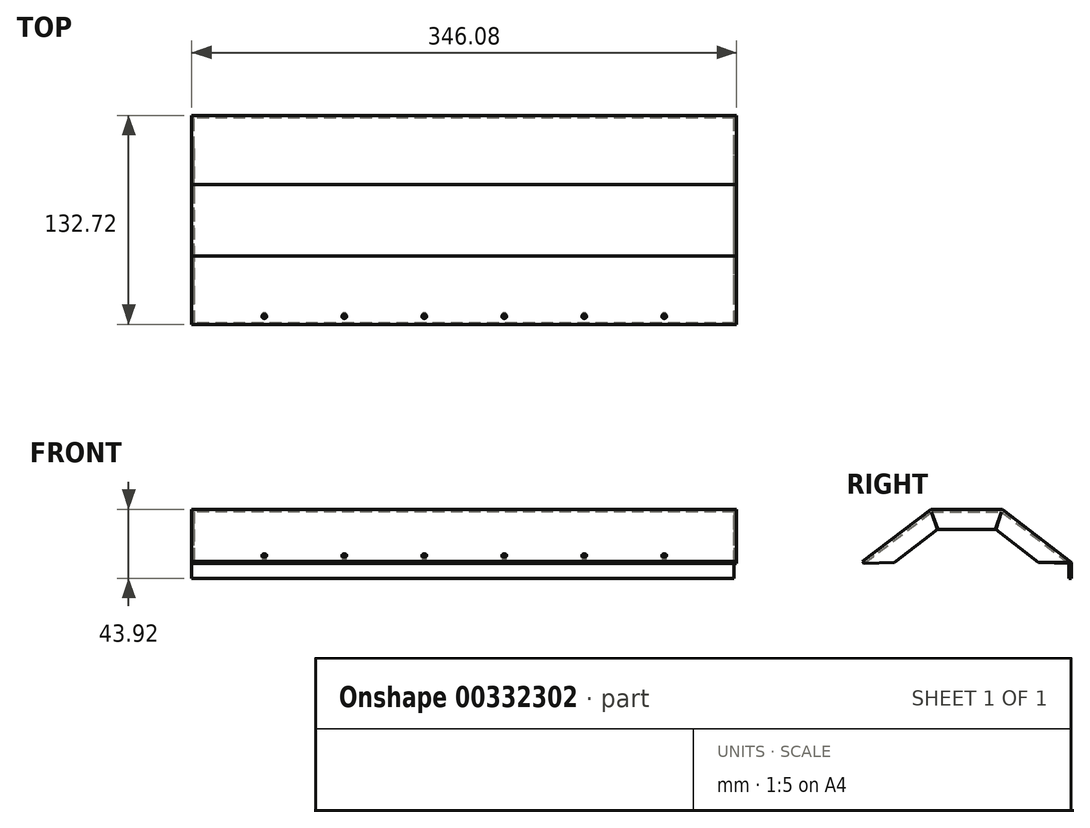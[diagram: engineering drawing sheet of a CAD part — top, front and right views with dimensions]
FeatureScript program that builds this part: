
annotation { "Feature Type Name" : "Feature", "Feature Type Description" : "" }
export const myFeature = defineFeature(function(context is Context, id is Id, definition is map)
    precondition{}
    {
        {
            var Q0;
            Q0=qCreatedBy(makeId("Right.planeOp"),FACE);
            var sketch = newSketch(context, id + "F0", { "sketchPlane" : qUnion([Q0])});
            skLineSegment(sketch, "E0", {"start": v(0, 0) * mm, "end": v(130.18, 0) * mm, "construction": true});
            skLineSegment(sketch, "E1", {"start": v(0, 0) * mm, "end": v(42.86, 32.8) * mm});
            skLineSegment(sketch, "E2", {"start": v(42.86, 32.8) * mm, "end": v(87.31, 32.8) * mm});
            skLineSegment(sketch, "E3", {"start": v(87.31, 32.8) * mm, "end": v(130.18, 0) * mm});
            skLineSegment(sketch, "E4", {"start": v(130.18, 0) * mm, "end": v(130.18, -9.53) * mm});
            skLineSegment(sketch, "E5", {"start": v(130.18, -9.53) * mm, "end": v(131.76, -9.53) * mm});
            skLineSegment(sketch, "E6.0", {"start": v(0, 1.59) * mm, "end": v(130.18, 1.59) * mm, "construction": true});
            skLineSegment(sketch, "E7", {"start": v(131.76, -9.53) * mm, "end": v(131.76, 0.78) * mm});
            skLineSegment(sketch, "E8.0", {"start": v(42.32, 34.4) * mm, "end": v(87.85, 34.4) * mm});
            skLineSegment(sketch, "E9.0", {"start": v(-0.96, 1.26) * mm, "end": v(42.32, 34.4) * mm});
            skLineSegment(sketch, "E10.0", {"start": v(87.85, 34.4) * mm, "end": v(131.76, 0.78) * mm});
            skLineSegment(sketch, "E11", {"start": v(-0.96, 1.26) * mm, "end": v(0, 0) * mm});
            skSolve(sketch);
        }
        {
            var Q0;
            Q0=makeQuery(id+"F0.imprint","IMPRINT",FACE,{"disambiguationData":[TD([[makeQuery(id+"F0.imprint","IMPRINT",EDGE,{"derivedFrom":sQuery(id+"F0.wireOp",EDGE,"E1")}),1.0]])]});
            extrude(context, id + "F1", {"entities" : qUnion([Q0]), "depth" : 342.9 * mm});
        }
        {
            var Q0;
            Q0=makeQuery(id+"F1.opExtrude","CAP_FACE",FACE,{"disambiguationData":[OSD([sQuery(id+"F0.wireOp",EDGE,"E1"),sQuery(id+"F0.wireOp",EDGE,"E2"),sQuery(id+"F0.wireOp",EDGE,"E3"),sQuery(id+"F0.wireOp",EDGE,"E4"),sQuery(id+"F0.wireOp",EDGE,"E5"),sQuery(id+"F0.wireOp",EDGE,"E7"),sQuery(id+"F0.wireOp",EDGE,"E8.0"),sQuery(id+"F0.wireOp",EDGE,"E9.0"),sQuery(id+"F0.wireOp",EDGE,"E10.0"),sQuery(id+"F0.wireOp",EDGE,"E11")])],"isStart":false});
            var sketch = newSketch(context, id + "F2", { "sketchPlane" : qUnion([Q0])});
            skLineSegment(sketch, "E12.0", {"start": v(19.36, 0.82) * mm, "end": v(46.42, 21.54) * mm});
            skLineSegment(sketch, "E13.0", {"start": v(46.88, 21.7) * mm, "end": v(83.3, 21.7) * mm});
            skLineSegment(sketch, "E14.0", {"start": v(83.75, 21.54) * mm, "end": v(110.81, 0.82) * mm});
            skLineSegment(sketch, "E15", {"start": v(19.36, 0.82) * mm, "end": v(0, 0) * mm});
            skLineSegment(sketch, "E16", {"start": v(46.88, 21.7) * mm, "end": v(42.86, 32.8) * mm});
            skLineSegment(sketch, "E17", {"start": v(42.86, 32.8) * mm, "end": v(46.42, 21.54) * mm});
            skLineSegment(sketch, "E18", {"start": v(83.3, 21.7) * mm, "end": v(87.31, 32.8) * mm});
            skLineSegment(sketch, "E19", {"start": v(87.31, 32.8) * mm, "end": v(83.75, 21.54) * mm});
            skLineSegment(sketch, "E20", {"start": v(130.18, 0) * mm, "end": v(123.42, -8.82) * mm, "construction": true});
            skLineSegment(sketch, "E21", {"start": v(110.81, 0.82) * mm, "end": v(130.18, 0) * mm});
            skSolve(sketch);
        }
        {
            var Q0;
            Q0=makeQuery(id+"F2.imprint","IMPRINT",FACE,{"disambiguationData":[TD([[makeQuery(id+"F2.imprint","IMPRINT",EDGE,{"derivedFrom":sQuery(id+"F2.wireOp",EDGE,"E12.0")}),1.0]])]});
            var Q1;
            Q1=makeQuery(id+"F2.imprint","IMPRINT",FACE,{"disambiguationData":[TD([[makeQuery(id+"F2.imprint","IMPRINT",EDGE,{"derivedFrom":sQuery(id+"F2.wireOp",EDGE,"E13.0")}),1.0]])]});
            var Q2;
            Q2=makeQuery(id+"F2.imprint","IMPRINT",FACE,{"disambiguationData":[TD([[makeQuery(id+"F2.imprint","IMPRINT",EDGE,{"derivedFrom":sQuery(id+"F2.wireOp",EDGE,"E14.0")}),1.0]])]});
            var Q3;
            Q3=makeQuery(id+"F2.imprint","IMPRINT",FACE,{"disambiguationData":[TD([[makeQuery(id+"F2.imprint","IMPRINT",EDGE,{"derivedFrom":makeQuery(id+"F1.opExtrude","CAP_EDGE",EDGE,{"disambiguationData":[OSD([sQuery(id+"F0.wireOp",EDGE,"E1")])],"isStart":false})}),1.0]])]});
            extrude(context, id + "F3", {"entities" : qUnion([Q0, Q1, Q2, Q3]), "depth" : 1.59 * mm});
        }
        {
            var Q0;
            Q0=makeQuery(id+"F3.opExtrude","SWEPT_FACE",FACE,{"disambiguationData":[OSD([sQuery(id+"F0.wireOp",EDGE,"E7")])]});
            var sketch = newSketch(context, id + "F4", { "sketchPlane" : qUnion([Q0])});
            skLineSegment(sketch, "E22.bottom", {"start": v(-344.49, 0.78) * mm, "end": v(-342.9, 0.78) * mm});
            skLineSegment(sketch, "E22.top", {"start": v(-344.49, -9.53) * mm, "end": v(-342.9, -9.53) * mm});
            skLineSegment(sketch, "E22.left", {"start": v(-344.49, 0.78) * mm, "end": v(-344.49, -9.53) * mm});
            skLineSegment(sketch, "E22.right", {"start": v(-342.9, 0.78) * mm, "end": v(-342.9, -9.53) * mm});
            skSolve(sketch);
        }
        {
            var Q0;
            Q0=makeQuery(id+"F4.imprint","IMPRINT",FACE,{"disambiguationData":[TD([[makeQuery(id+"F4.imprint","IMPRINT",EDGE,{"derivedFrom":sQuery(id+"F4.wireOp",EDGE,"E22.bottom")}),-1.0]])]});
            extrude(context, id + "F5", {"entities" : qUnion([Q0]), "operationType" : NewBodyOperationType.REMOVE, "oppositeDirection" : true, "depth" : 25.4 * mm});
        }
        {
            var Q0;
            Q0=makeQuery(id+"F1.opExtrude","CAP_FACE",FACE,{"disambiguationData":[OSD([sQuery(id+"F0.wireOp",EDGE,"E1"),sQuery(id+"F0.wireOp",EDGE,"E2"),sQuery(id+"F0.wireOp",EDGE,"E3"),sQuery(id+"F0.wireOp",EDGE,"E4"),sQuery(id+"F0.wireOp",EDGE,"E5"),sQuery(id+"F0.wireOp",EDGE,"E7"),sQuery(id+"F0.wireOp",EDGE,"E8.0"),sQuery(id+"F0.wireOp",EDGE,"E9.0"),sQuery(id+"F0.wireOp",EDGE,"E10.0"),sQuery(id+"F0.wireOp",EDGE,"E11")])],"isStart":true});
            var sketch = newSketch(context, id + "F6", { "sketchPlane" : qUnion([Q0])});
            skLineSegment(sketch, "E23.0", {"start": v(-110.81, 0.82) * mm, "end": v(-83.75, 21.54) * mm});
            skLineSegment(sketch, "E24.0", {"start": v(-83.3, 21.7) * mm, "end": v(-46.88, 21.7) * mm});
            skLineSegment(sketch, "E25.0", {"start": v(-46.42, 21.54) * mm, "end": v(-19.36, 0.82) * mm});
            skLineSegment(sketch, "E26", {"start": v(-110.81, 0.82) * mm, "end": v(-130.18, 0) * mm});
            skLineSegment(sketch, "E27", {"start": v(-83.3, 21.7) * mm, "end": v(-87.31, 32.8) * mm});
            skLineSegment(sketch, "E28", {"start": v(-87.31, 32.8) * mm, "end": v(-83.75, 21.54) * mm});
            skLineSegment(sketch, "E29", {"start": v(-46.88, 21.7) * mm, "end": v(-42.86, 32.8) * mm});
            skLineSegment(sketch, "E30", {"start": v(-42.86, 32.8) * mm, "end": v(-46.42, 21.54) * mm});
            skLineSegment(sketch, "E31", {"start": v(0, 0) * mm, "end": v(-6.75, -8.82) * mm, "construction": true});
            skLineSegment(sketch, "E32", {"start": v(-19.36, 0.82) * mm, "end": v(0, 0) * mm});
            skSolve(sketch);
        }
        {
            var Q0;
            Q0=makeQuery(id+"F6.imprint","IMPRINT",FACE,{"disambiguationData":[TD([[makeQuery(id+"F6.imprint","IMPRINT",EDGE,{"derivedFrom":sQuery(id+"F6.wireOp",EDGE,"E23.0")}),1.0]])]});
            var Q1;
            Q1=makeQuery(id+"F6.imprint","IMPRINT",FACE,{"disambiguationData":[TD([[makeQuery(id+"F6.imprint","IMPRINT",EDGE,{"derivedFrom":sQuery(id+"F6.wireOp",EDGE,"E24.0")}),1.0]])]});
            var Q2;
            Q2=makeQuery(id+"F6.imprint","IMPRINT",FACE,{"disambiguationData":[TD([[makeQuery(id+"F6.imprint","IMPRINT",EDGE,{"derivedFrom":sQuery(id+"F6.wireOp",EDGE,"E25.0")}),1.0]])]});
            var Q3;
            Q3=makeQuery(id+"F6.imprint","IMPRINT",FACE,{"disambiguationData":[TD([[makeQuery(id+"F6.imprint","IMPRINT",EDGE,{"derivedFrom":makeQuery(id+"F1.opExtrude","CAP_EDGE",EDGE,{"disambiguationData":[OSD([sQuery(id+"F0.wireOp",EDGE,"E1")])],"isStart":true})}),-1.0]])]});
            extrude(context, id + "F7", {"entities" : qUnion([Q0, Q1, Q2, Q3]), "operationType" : NewBodyOperationType.ADD, "depth" : 1.59 * mm});
        }
        {
            var Q0;
            Q0=makeQuery(id+"F1.opExtrude","SWEPT_BODY",BODY,{"disambiguationData":[OSD([sQuery(id+"F0.wireOp",EDGE,"E1"),sQuery(id+"F0.wireOp",EDGE,"E2"),sQuery(id+"F0.wireOp",EDGE,"E3"),sQuery(id+"F0.wireOp",EDGE,"E4"),sQuery(id+"F0.wireOp",EDGE,"E5"),sQuery(id+"F0.wireOp",EDGE,"E7"),sQuery(id+"F0.wireOp",EDGE,"E8.0"),sQuery(id+"F0.wireOp",EDGE,"E9.0"),sQuery(id+"F0.wireOp",EDGE,"E10.0"),sQuery(id+"F0.wireOp",EDGE,"E11")])]});
            var Q1;
            Q1=makeQuery(id+"F3.opExtrude","SWEPT_BODY",BODY,{"disambiguationData":[OSD([sQuery(id+"F0.wireOp",EDGE,"E4"),sQuery(id+"F0.wireOp",EDGE,"E5"),sQuery(id+"F0.wireOp",EDGE,"E7"),sQuery(id+"F0.wireOp",EDGE,"E8.0"),sQuery(id+"F0.wireOp",EDGE,"E9.0"),sQuery(id+"F0.wireOp",EDGE,"E10.0"),sQuery(id+"F0.wireOp",EDGE,"E11"),sQuery(id+"F2.wireOp",EDGE,"E12.0"),sQuery(id+"F2.wireOp",EDGE,"E13.0"),sQuery(id+"F2.wireOp",EDGE,"E14.0"),sQuery(id+"F2.wireOp",EDGE,"E15"),sQuery(id+"F2.wireOp",EDGE,"E16"),sQuery(id+"F2.wireOp",EDGE,"E17"),sQuery(id+"F2.wireOp",EDGE,"E18"),sQuery(id+"F2.wireOp",EDGE,"E19"),sQuery(id+"F2.wireOp",EDGE,"E21")])]});
            booleanBodies(context, id + "F8", {"operationType" : BooleanOperationType.UNION, "tools" : qUnion([Q0, Q1])});
        }
        {
            var Q0;
            {var subQ0=sQuery(id+"F0.wireOp",EDGE,"E9.0");Q0=makeQuery(id+"F8.opBoolean","MERGE",FACE,{"derivedFrom":[makeQuery(id+"F3.opExtrude","SWEPT_FACE",FACE,{"disambiguationData":[OSD([subQ0])]}),makeQuery(id+"F7.boolean.opBoolean","MERGE",FACE,{"derivedFrom":[makeQuery(id+"F1.opExtrude","SWEPT_FACE",FACE,{"disambiguationData":[OSD([subQ0])]}),makeQuery(id+"F7.opExtrude","SWEPT_FACE",FACE,{"disambiguationData":[OSD([subQ0])]})]})]});}
            var sketch = newSketch(context, id + "F9", { "sketchPlane" : qUnion([Q0])});
            skLineSegment(sketch, "E33", {"start": v(-1.59, 0) * mm, "end": v(19.05, 0) * mm, "construction": true});
            skLineSegment(sketch, "E34", {"start": v(19.05, 0) * mm, "end": v(323.85, 0) * mm, "construction": true});
            skLineSegment(sketch, "E35", {"start": v(323.85, 0) * mm, "end": v(344.49, 0) * mm});
            skLineSegment(sketch, "E36", {"start": v(19.05, 0) * mm, "end": v(19.05, 12.7) * mm, "construction": true});
            skLineSegment(sketch, "E37", {"start": v(19.05, 0) * mm, "end": v(19.05, 23.46) * mm, "construction": true});
            skPoint(sketch, "E37.endSnap0", {"position": v(19.05, 6.35) * mm});
            skLineSegment(sketch, "E38.0", {"start": v(44.45, 0) * mm, "end": v(44.45, 23.46) * mm, "construction": true});
            skLineSegment(sketch, "E39.0", {"start": v(95.25, 0) * mm, "end": v(95.25, 23.46) * mm, "construction": true});
            skLineSegment(sketch, "E40.0", {"start": v(146.05, 0) * mm, "end": v(146.05, 23.46) * mm, "construction": true});
            skLineSegment(sketch, "E41.0", {"start": v(196.85, 0) * mm, "end": v(196.85, 23.46) * mm, "construction": true});
            skLineSegment(sketch, "E42.0", {"start": v(247.65, 0) * mm, "end": v(247.65, 23.46) * mm, "construction": true});
            skLineSegment(sketch, "E43.0", {"start": v(298.45, 0) * mm, "end": v(298.45, 23.46) * mm, "construction": true});
            skLineSegment(sketch, "E44", {"start": v(19.05, 0) * mm, "end": v(19.05, 6.35) * mm, "construction": true});
            skLineSegment(sketch, "E45", {"start": v(19.05, 6.35) * mm, "end": v(337.9, 6.35) * mm, "construction": true});
            skCircle(sketch, "E46", {"center": v(44.45, 6.35) * mm, "radius": 1.59 * mm});
            skCircle(sketch, "E47", {"center": v(95.25, 6.35) * mm, "radius": 1.59 * mm});
            skCircle(sketch, "E48", {"center": v(146.05, 6.35) * mm, "radius": 1.59 * mm});
            skCircle(sketch, "E49", {"center": v(196.85, 6.35) * mm, "radius": 1.59 * mm});
            skCircle(sketch, "E50", {"center": v(247.65, 6.35) * mm, "radius": 1.59 * mm});
            skCircle(sketch, "E51", {"center": v(298.45, 6.35) * mm, "radius": 1.59 * mm});
            skSolve(sketch);
        }
        {
            var Q0;
            Q0=qSketchRegion(id+"F9",true);
            extrude(context, id + "F10", {"entities" : qUnion([Q0]), "operationType" : NewBodyOperationType.REMOVE, "endBound" : BoundingType.UP_TO_NEXT, "oppositeDirection" : true, "depth" : 25.4 * mm});
        }
    });
